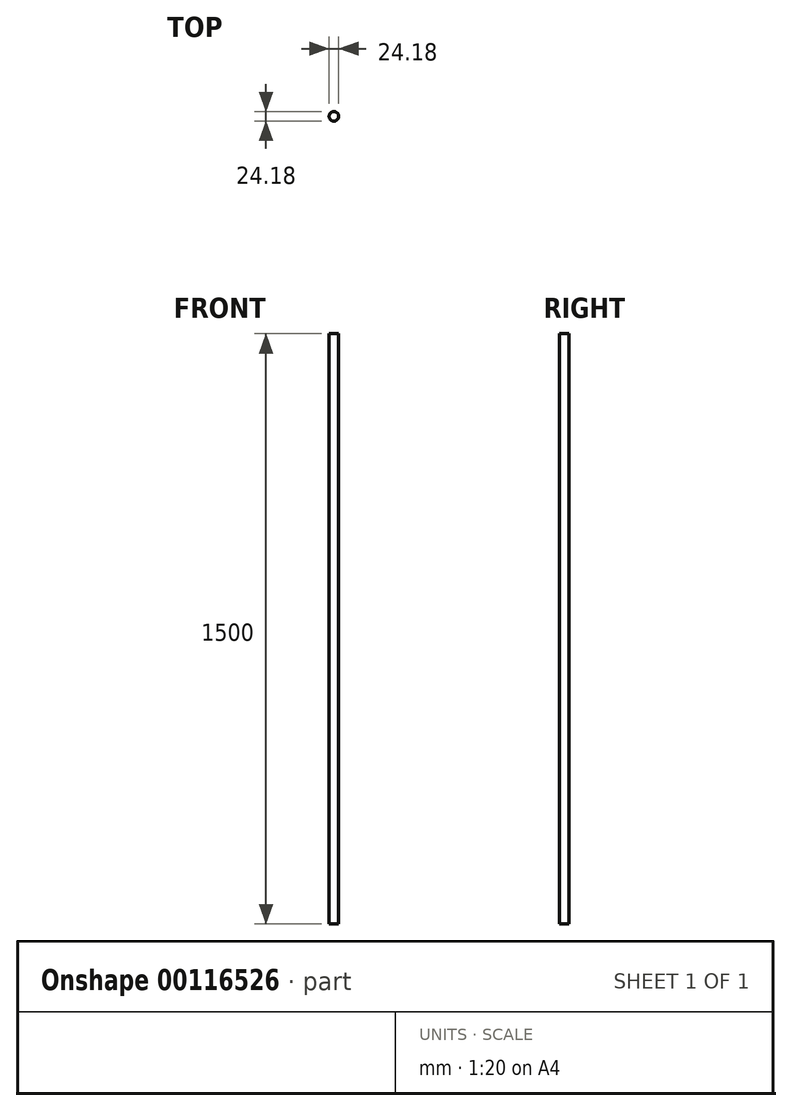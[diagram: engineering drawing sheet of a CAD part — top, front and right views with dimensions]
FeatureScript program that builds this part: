
annotation { "Feature Type Name" : "Feature", "Feature Type Description" : "" }
export const myFeature = defineFeature(function(context is Context, id is Id, definition is map)
    precondition{}
    {
        {
            var Q0;
            Q0=qCreatedBy(makeId("Top.planeOp"),FACE);
            var sketch = newSketch(context, id + "F0", { "sketchPlane" : qUnion([Q0])});
            skCircle(sketch, "E0", {"center": v(0, 0) * mm, "radius": 12.1 * mm});
            skSolve(sketch);
        }
        {
            var Q0;
            Q0=qSketchRegion(id+"F0",true);
            var Q1;
            Q1=makeQuery(id+"F0.imprint","IMPRINT",FACE,{"disambiguationData":[TD([[makeQuery(id+"F0.imprint","IMPRINT",EDGE,{"derivedFrom":sQuery(id+"F0.wireOp",EDGE,"E0")}),1.0]])]});
            extrude(context, id + "F1", {"entities" : qUnion([Q0, Q1]), "depth" : 1500 * mm});
        }
    });
